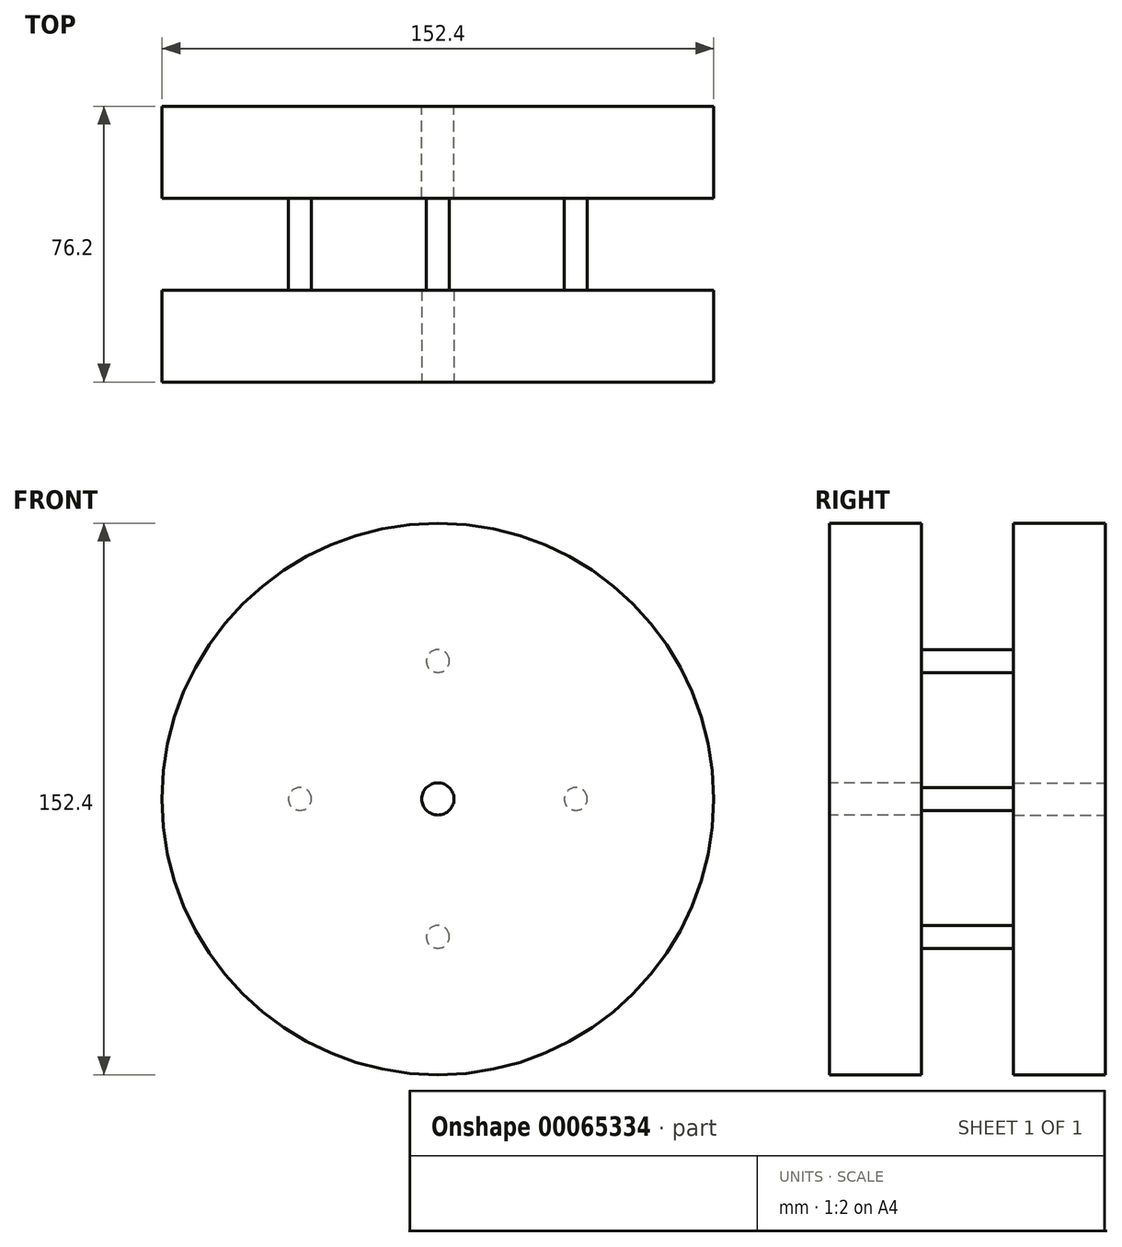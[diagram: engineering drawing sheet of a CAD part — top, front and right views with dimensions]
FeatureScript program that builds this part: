
annotation { "Feature Type Name" : "Feature", "Feature Type Description" : "" }
export const myFeature = defineFeature(function(context is Context, id is Id, definition is map)
    precondition{}
    {
        {
            var Q0;
            Q0=qCreatedBy(makeId("Front.planeOp"),FACE);
            var sketch = newSketch(context, id + "F0", { "sketchPlane" : qUnion([Q0])});
            skCircle(sketch, "E0", {"center": v(0, 0) * mm, "radius": 76.2 * mm});
            skSolve(sketch);
        }
        {
            var Q0;
            Q0=makeQuery(id+"F0.imprint","IMPRINT",FACE,{"disambiguationData":[TD([[makeQuery(id+"F0.imprint","IMPRINT",EDGE,{"derivedFrom":sQuery(id+"F0.wireOp",EDGE,"E0")}),1.0]])]});
            var sketch = newSketch(context, id + "F1", { "sketchPlane" : qUnion([Q0])});
            skCircle(sketch, "E1", {"center": v(0, 0) * mm, "radius": 4.45 * mm});
            skSolve(sketch);
        }
        {
            var Q0;
            Q0 = qSketchRegion(id + "F0", true);
            extrude(context, id + "F2", {"entities" : qUnion([Q0]), "depth" : 25.4 * mm});
        }
        {
            var Q0;
            Q0 = qSketchRegion(id + "F1", true);
            extrude(context, id + "F3", {"entities" : qUnion([Q0]), "operationType" : NewBodyOperationType.REMOVE, "depth" : 25.4 * mm});
        }
        {
            var Q0;
            Q0=makeQuery(id+"F2.opExtrude","CAP_FACE",FACE,{"disambiguationData":[OSD([sQuery(id+"F0.wireOp",EDGE,"E0")])],"isStart":false});
            var sketch = newSketch(context, id + "F4", { "sketchPlane" : qUnion([Q0])});
            skCircle(sketch, "E2", {"center": v(38.1, 0) * mm, "radius": 3.18 * mm});
            skCircle(sketch, "E3", {"center": v(0, 38.1) * mm, "radius": 3.18 * mm});
            skCircle(sketch, "E4", {"center": v(-38.1, 0) * mm, "radius": 3.18 * mm});
            skCircle(sketch, "E5", {"center": v(0, -38.1) * mm, "radius": 3.18 * mm});
            skSolve(sketch);
        }
        {
            var Q0;
            Q0 = qSketchRegion(id + "F4", true);
            extrude(context, id + "F5", {"entities" : qUnion([Q0]), "operationType" : NewBodyOperationType.ADD, "depth" : 25.4 * mm});
        }
        {
            var Q0;
            Q0=makeQuery(id+"F5.opExtrude","CAP_FACE",FACE,{"disambiguationData":[OSD([sQuery(id+"F4.wireOp",EDGE,"E4")])],"isStart":false});
            var sketch = newSketch(context, id + "F6", { "sketchPlane" : qUnion([Q0])});
            skCircle(sketch, "E6", {"center": v(0, 0) * mm, "radius": 76.2 * mm});
            skSolve(sketch);
        }
        {
            var Q0;
            Q0 = qSketchRegion(id + "F6", true);
            extrude(context, id + "F7", {"entities" : qUnion([Q0]), "operationType" : NewBodyOperationType.ADD, "depth" : 25.4 * mm});
        }
        {
            var Q0;
            Q0=makeQuery(id+"F7.opExtrude","CAP_FACE",FACE,{"disambiguationData":[OSD([sQuery(id+"F6.wireOp",EDGE,"E6")])],"isStart":false});
            var sketch = newSketch(context, id + "F8", { "sketchPlane" : qUnion([Q0])});
            skCircle(sketch, "E7", {"center": v(0, 0) * mm, "radius": 4.44 * mm});
            skSolve(sketch);
        }
        {
            var Q0;
            Q0 = qSketchRegion(id + "F8", true);
            extrude(context, id + "F9", {"entities" : qUnion([Q0]), "operationType" : NewBodyOperationType.REMOVE, "oppositeDirection" : true, "depth" : 25.4 * mm});
        }
    });
